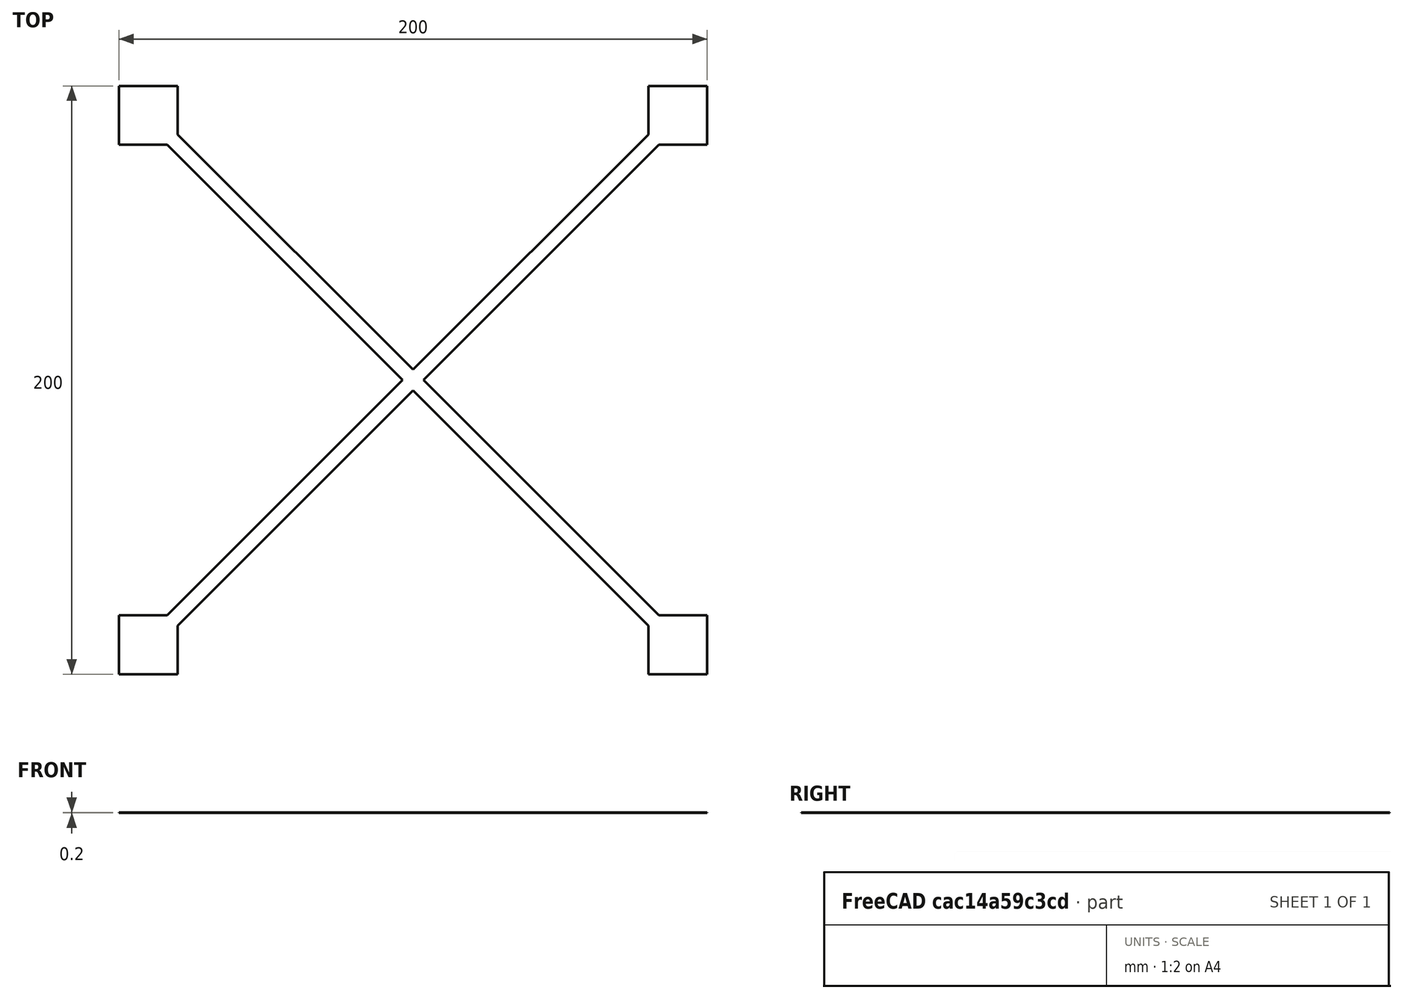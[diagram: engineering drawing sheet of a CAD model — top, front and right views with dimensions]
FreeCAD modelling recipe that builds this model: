
FCSTD DOCUMENT  (FreeCAD 0.20R27319 (Git))
Label: Boxes
License: All rights reserved
LicenseURL: http://en.wikipedia.org/wiki/All_rights_reserved
objects: Sketcher::SketchObject×1, Spreadsheet::Sheet×1, PartDesign::Pad×1, PartDesign::Body×1
note: 4 computed .brp shape members not serialized (recipe doc carries the construction recipe); baked Part::Feature solids carry a one-line shape summary decoded from their .brp

FEATURE [Sketcher::SketchObject] Sketch
  FullyConstrained = true
  MapMode = 5
  Support = -> [XY_Plane]
  expr: Constraints[49] = Spreadsheet.BoxSize
  expr: Constraints[50] = Spreadsheet.Width
  expr: Constraints[63] = Spreadsheet.BoxSize
  expr: Constraints[91] = Spreadsheet.CrossSize
  sketch-geometry (38):
    g0: LineSegment StartX=-100 StartY=100 StartZ=0 EndX=-100 EndY=-100 EndZ=0
    g1: LineSegment StartX=-100 StartY=-100 StartZ=0 EndX=100 EndY=-100 EndZ=0
    g2: LineSegment StartX=100 StartY=-100 StartZ=0 EndX=100 EndY=100 EndZ=0
    g3: LineSegment StartX=100 StartY=100 StartZ=0 EndX=-100 EndY=100 EndZ=0
    g4: GeomPoint X=0 Y=0 Z=0
    g5: LineSegment StartX=100 StartY=100 StartZ=0 EndX=80 EndY=100 EndZ=0
    g6: LineSegment StartX=80 StartY=100 StartZ=0 EndX=80 EndY=83.5355 EndZ=0
    g7: LineSegment StartX=83.5355 StartY=80 StartZ=0 EndX=100 EndY=80 EndZ=0
    g8: LineSegment StartX=100 StartY=80 StartZ=0 EndX=100 EndY=100 EndZ=0
    g9: LineSegment StartX=-100 StartY=-100 StartZ=0 EndX=-80 EndY=-100 EndZ=0
    g10: LineSegment StartX=-80 StartY=-100 StartZ=0 EndX=-80 EndY=-83.5355 EndZ=0
    g11: LineSegment StartX=-83.5355 StartY=-80 StartZ=0 EndX=-100 EndY=-80 EndZ=0
    g12: LineSegment StartX=-100 StartY=-80 StartZ=0 EndX=-100 EndY=-100 EndZ=0
    g13: LineSegment StartX=100 StartY=-100 StartZ=0 EndX=80 EndY=-100 EndZ=0
    g14: LineSegment StartX=80 StartY=-100 StartZ=0 EndX=80 EndY=-83.5355 EndZ=0
    g15: LineSegment StartX=83.5356 StartY=-80 StartZ=0 EndX=100 EndY=-80 EndZ=0
    g16: LineSegment StartX=100 StartY=-80 StartZ=0 EndX=100 EndY=-100 EndZ=0
    g17: LineSegment StartX=-100 StartY=100 StartZ=0 EndX=-80 EndY=100 EndZ=0
    g18: LineSegment StartX=-80 StartY=100 StartZ=0 EndX=-80 EndY=83.5355 EndZ=0
    g19: LineSegment StartX=-83.5355 StartY=80 StartZ=0 EndX=-100 EndY=80 EndZ=0
    g20: LineSegment StartX=-100 StartY=80 StartZ=0 EndX=-100 EndY=100 EndZ=0
    g21: LineSegment StartX=83.5356 StartY=-80 StartZ=0 EndX=3.53553 EndY=0 EndZ=0
    g22: LineSegment StartX=-80 StartY=83.5355 StartZ=0 EndX=-83.5355 EndY=80 EndZ=0
    g23: LineSegment StartX=-83.5355 StartY=80 StartZ=0 EndX=-3.53553 EndY=0 EndZ=0
    g24: LineSegment StartX=80 StartY=-83.5355 StartZ=0 EndX=83.5356 EndY=-80 EndZ=0
    g25: LineSegment StartX=-83.5355 StartY=-80 StartZ=0 EndX=-3.53553 EndY=0 EndZ=0
    g26: LineSegment StartX=80 StartY=83.5355 StartZ=0 EndX=83.5355 EndY=80 EndZ=0
    g27: LineSegment StartX=83.5355 StartY=80 StartZ=0 EndX=3.53553 EndY=0 EndZ=0
    g28: LineSegment StartX=-80 StartY=-83.5355 StartZ=0 EndX=-83.5355 EndY=-80 EndZ=0
    g29: LineSegment StartX=3.53553 StartY=0 StartZ=0 EndX=0 EndY=3.53553 EndZ=0
    g30: LineSegment StartX=-1e-16 StartY=3.53553 StartZ=0 EndX=-3.53553 EndY=0 EndZ=0
    g31: LineSegment StartX=-3.53553 StartY=-1e-16 StartZ=0 EndX=9e-16 EndY=-3.53553 EndZ=0
    g32: LineSegment StartX=9e-16 StartY=-3.53553 StartZ=0 EndX=3.53553 EndY=0 EndZ=0
    g33: Circle CenterX=0 CenterY=0 CenterZ=0 NormalX=0 NormalY=0 NormalZ=1 AngleXU=0 Radius=3.53553
    g34: LineSegment StartX=-1e-16 StartY=3.53553 StartZ=0 EndX=80 EndY=83.5355 EndZ=0
    g35: LineSegment StartX=9e-16 StartY=-3.53553 StartZ=0 EndX=-80 EndY=-83.5355 EndZ=0
    g36: LineSegment StartX=-1e-16 StartY=3.53553 StartZ=0 EndX=-80 EndY=83.5355 EndZ=0
    g37: LineSegment StartX=9e-16 StartY=-3.53553 StartZ=0 EndX=80 EndY=-83.5355 EndZ=0
  constraints (99):
    c: Coincident(g0,g1)
    c: Coincident(g1,g2)
    c: Coincident(g2,g3)
    c: Horizontal(g1)
    c: Horizontal(g3)
    c: Vertical(g0)
    c: Vertical(g2)
    c: Symmetric(g1,g0,g4)
    c: Coincident(g4,g-1)
    c: Equal(g2,g3)
    c: Coincident(g5,g6)
    c: Coincident(g7,g8)
    c: Coincident(g8,g5)
    c: Horizontal(g5)
    c: Horizontal(g7)
    c: Vertical(g6)
    c: Vertical(g8)
    c: Coincident(g5,g2)
    c: Coincident(g9,g10)
    c: Coincident(g11,g12)
    c: Coincident(g12,g9)
    c: Horizontal(g9)
    c: Horizontal(g11)
    c: Vertical(g10)
    c: Vertical(g12)
    c: Coincident(g9,g0)
    c: Coincident(g13,g14)
    c: Coincident(g15,g16)
    c: Coincident(g16,g13)
    c: Horizontal(g13)
    c: Horizontal(g15)
    c: Vertical(g14)
    c: Vertical(g16)
    c: Coincident(g13,g1)
    c: Coincident(g17,g18)
    c: Coincident(g19,g20)
    c: Coincident(g20,g17)
    c: Horizontal(g17)
    c: Horizontal(g19)
    c: Vertical(g18)
    c: Vertical(g20)
    c: Coincident(g17,g0)
    c: Coincident(g36,g22)
    c: Coincident(g22,g23)
    c: Coincident(g37,g24)
    c: Coincident(g24,g21)
    c: Equal(g22,g24)
    c: Equal(g17,g5)
    c: Coincident(g17,g3)
    c: Distance(g20) = 20
    c: Distance(g3) = 200
    c: Coincident(g34,g26)
    c: Coincident(g26,g27)
    c: Coincident(g35,g28)
    c: Coincident(g28,g25)
    c: Perpendicular(g28,g25)
    c: Parallel(g25,g27)
    c: Perpendicular(g26,g25)
    c: PointOnObject(g34,g6)
    c: Coincident(g11,g25)
    c: Coincident(g10,g35)
    c: Coincident(g18,g36)
    c: Coincident(g19,g22)
    c: Distance(g17) = 20
    c: Equal(g16,g12)
    c: Equal(g12,g20)
    c: PointOnObject(g6,g26)
    c: Coincident(g7,g26)
    c: Coincident(g15,g21)
    c: Coincident(g29,g30)
    c: Coincident(g30,g31)
    c: Coincident(g31,g32)
    c: Coincident(g32,g29)
    c: Equal(g29,g30)
    c: Equal(g29,g31)
    c: Equal(g29,g32)
    c: PointOnObject(g29,g33)
    c: PointOnObject(g30,g33)
    c: PointOnObject(g31,g33)
    c: PointOnObject(g32,g33)
    c: Coincident(g33,g4)
    c: PointOnObject(g32,g-1)
    c: PointOnObject(g29,g25)
    c: Coincident(g21,g27)
    c: Coincident(g37,g35)
    c: Coincident(g35,g31)
    c: Coincident(g21,g29)
    c: Coincident(g25,g23)
    c: Coincident(g25,g30)
    c: Coincident(g36,g29)
    c: Coincident(g36,g34)
    c: Distance(g30) = 5
    c: Parallel(g36,g23)
    c: Parallel(g34,g27)
    c: Parallel(g25,g35)
    c: Parallel(g37,g21)
    c: Coincident(g14,g37)
    c: Equal(g24,g32)
    c: Equal(g5,g13)
FEATURE [Spreadsheet::Sheet] Spreadsheet
  cells = A1=Height; B1(Height)=200; A2=Width; B2(Width)==B1; A3=BoxSize; B3(BoxSize)=20; A4=CrossSize; B4(CrossSize)=5
FEATURE [PartDesign::Pad] Pad
  Direction = (0,0,1)
  Length = 0.2
  Length2 = 10
  Profile = -> Sketch
  ReferenceAxis = -> Sketch [N_Axis]
  Type = 0
FEATURE [PartDesign::Body] Body
  Group = -> [Sketch,Pad]
  Origin = -> Origin
  Tip = -> Pad
